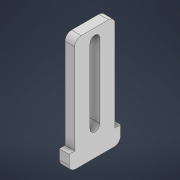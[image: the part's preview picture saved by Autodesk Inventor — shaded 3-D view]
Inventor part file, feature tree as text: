
AUTODESK INVENTOR PART (.ipt)
format: ipt  version: 2021 (Build 250183000, 183)  size: 123,392 bytes
history: native  units: mm
features: extrude x2, sketch x2, fillet x1
ambient origin geometry x8: Origin, YZ Plane, XZ Plane, XY Plane, X Axis, Y Axis, Z Axis, Center Point
bodies: Solid1 (feature_tree)
feature tree (5):
  extrude  "Extrusion1"  Depth=16.0mm
  extrude  "Extrusion2"  Depth=5.0mm
  fillet  "Fillet1"  Radius=3.0mm
  sketch  "Sketch1"  dims[d0=35.0mm d1=16.0mm]
  sketch  "Sketch2"  dims[d2=3.0mm d3=0.0mm d4=5.0mm d5=3.0mm d6=23.0mm d7=0.0mm d8=0.0mm d9=6.25mm d10=2.0mm]
